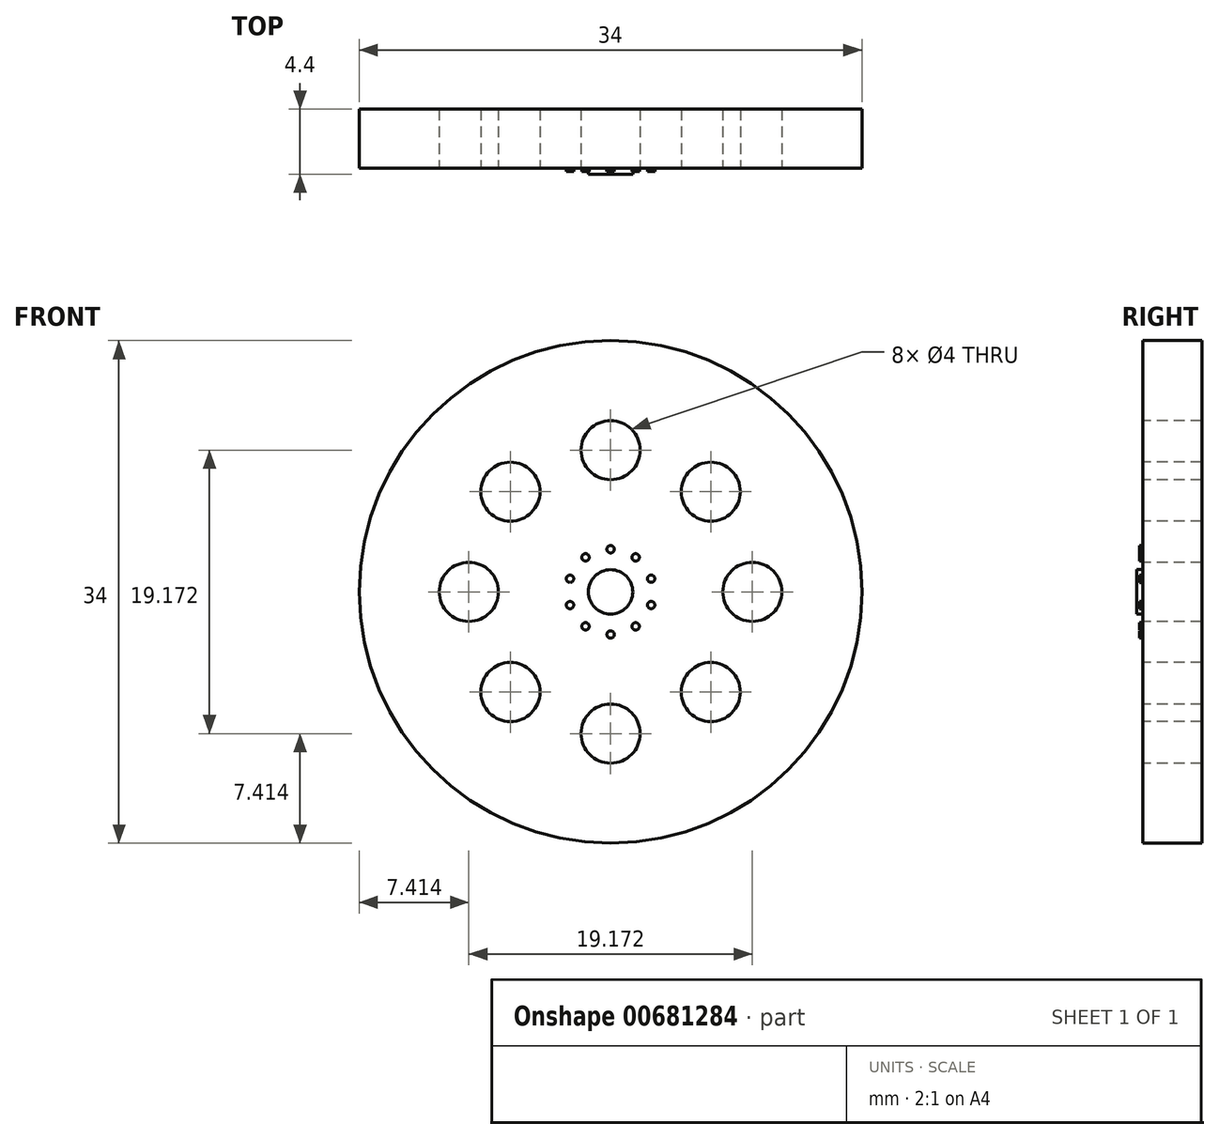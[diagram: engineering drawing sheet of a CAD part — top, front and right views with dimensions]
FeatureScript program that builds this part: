
annotation { "Feature Type Name" : "Feature", "Feature Type Description" : "" }
export const myFeature = defineFeature(function(context is Context, id is Id, definition is map)
    precondition{}
    {
        {
            var Q0;
            Q0=qCreatedBy(makeId("Front.planeOp"),FACE);
            var sketch = newSketch(context, id + "F0", { "sketchPlane" : qUnion([Q0])});
            skCircle(sketch, "E0", {"center": v(0, 0) * mm, "radius": 17 * mm});
            skSolve(sketch);
        }
        {
            var Q0;
            Q0 = qSketchRegion(id + "F0", true);
            extrude(context, id + "F1", {"entities" : qUnion([Q0]), "endBound" : BoundingType.SYMMETRIC, "depth" : 4 * mm, "offsetDistance" : 25 * mm});
        }
        {
            var Q0;
            Q0=makeQuery(id+"F1.opExtrude","CAP_FACE",FACE,{"disambiguationData":[OSD([sQuery(id+"F0.wireOp",EDGE,"E0")])],"isStart":false});
            var sketch = newSketch(context, id + "F2", { "sketchPlane" : qUnion([Q0])});
            skCircle(sketch, "E1", {"center": v(0, 9.59) * mm, "radius": 2 * mm});
            skCircle(sketch, "E2.1.0", {"center": v(-6.78, 6.78) * mm, "radius": 2 * mm});
            skCircle(sketch, "E2.2.0", {"center": v(-9.59, 0) * mm, "radius": 2 * mm});
            skCircle(sketch, "E2.3.0", {"center": v(-6.78, -6.78) * mm, "radius": 2 * mm});
            skCircle(sketch, "E2.4.0", {"center": v(0, -9.59) * mm, "radius": 2 * mm});
            skCircle(sketch, "E2.5.0", {"center": v(6.78, -6.78) * mm, "radius": 2 * mm});
            skCircle(sketch, "E2.6.0", {"center": v(9.59, 0) * mm, "radius": 2 * mm});
            skCircle(sketch, "E2.7.0", {"center": v(6.78, 6.78) * mm, "radius": 2 * mm});
            skPoint(sketch, "E2.center", {"position": v(0, 0) * mm});
            skSolve(sketch);
        }
        {
            var Q0;
            Q0=makeQuery(id+"F2.imprint","IMPRINT",FACE,{"disambiguationData":[TD([[makeQuery(id+"F2.imprint","IMPRINT",EDGE,{"derivedFrom":sQuery(id+"F2.wireOp",EDGE,"E2.1.0")}),1.0]])]});
            var Q1;
            Q1=makeQuery(id+"F2.imprint","IMPRINT",FACE,{"disambiguationData":[TD([[makeQuery(id+"F2.imprint","IMPRINT",EDGE,{"derivedFrom":sQuery(id+"F2.wireOp",EDGE,"E2.2.0")}),1.0]])]});
            var Q2;
            Q2=makeQuery(id+"F2.imprint","IMPRINT",FACE,{"disambiguationData":[TD([[makeQuery(id+"F2.imprint","IMPRINT",EDGE,{"derivedFrom":sQuery(id+"F2.wireOp",EDGE,"E2.3.0")}),1.0]])]});
            var Q3;
            Q3=makeQuery(id+"F2.imprint","IMPRINT",FACE,{"disambiguationData":[TD([[makeQuery(id+"F2.imprint","IMPRINT",EDGE,{"derivedFrom":sQuery(id+"F2.wireOp",EDGE,"E2.4.0")}),1.0]])]});
            var Q4;
            Q4=makeQuery(id+"F2.imprint","IMPRINT",FACE,{"disambiguationData":[TD([[makeQuery(id+"F2.imprint","IMPRINT",EDGE,{"derivedFrom":sQuery(id+"F2.wireOp",EDGE,"E2.5.0")}),1.0]])]});
            var Q5;
            Q5=makeQuery(id+"F2.imprint","IMPRINT",FACE,{"disambiguationData":[TD([[makeQuery(id+"F2.imprint","IMPRINT",EDGE,{"derivedFrom":sQuery(id+"F2.wireOp",EDGE,"E2.6.0")}),1.0]])]});
            var Q6;
            Q6=makeQuery(id+"F2.imprint","IMPRINT",FACE,{"disambiguationData":[TD([[makeQuery(id+"F2.imprint","IMPRINT",EDGE,{"derivedFrom":sQuery(id+"F2.wireOp",EDGE,"E2.7.0")}),1.0]])]});
            var Q7;
            Q7=makeQuery(id+"F2.imprint","IMPRINT",FACE,{"disambiguationData":[TD([[makeQuery(id+"F2.imprint","IMPRINT",EDGE,{"derivedFrom":sQuery(id+"F2.wireOp",EDGE,"E1")}),1.0]])]});
            extrude(context, id + "F3", {"entities" : qUnion([Q0, Q1, Q2, Q3, Q4, Q5, Q6, Q7]), "operationType" : NewBodyOperationType.REMOVE, "oppositeDirection" : true, "depth" : 4 * mm, "offsetDistance" : 25 * mm});
        }
        {
            var Q0;
            Q0=makeQuery(id+"F1.opExtrude","CAP_FACE",FACE,{"disambiguationData":[OSD([sQuery(id+"F0.wireOp",EDGE,"E0")])],"isStart":false});
            var sketch = newSketch(context, id + "F4", { "sketchPlane" : qUnion([Q0])});
            skCircle(sketch, "E3", {"center": v(0, 0) * mm, "radius": 1.84 * mm});
            skCircle(sketch, "E4", {"center": v(0, 2.88) * mm, "radius": 0.25 * mm});
            skCircle(sketch, "E5.1.0", {"center": v(-1.7, 2.33) * mm, "radius": 0.25 * mm});
            skCircle(sketch, "E5.2.0", {"center": v(-2.74, 0.9) * mm, "radius": 0.25 * mm});
            skCircle(sketch, "E5.3.0", {"center": v(-2.74, -0.9) * mm, "radius": 0.25 * mm});
            skCircle(sketch, "E5.4.0", {"center": v(-1.7, -2.33) * mm, "radius": 0.25 * mm});
            skCircle(sketch, "E5.5.0", {"center": v(0, -2.88) * mm, "radius": 0.25 * mm});
            skCircle(sketch, "E5.6.0", {"center": v(1.7, -2.33) * mm, "radius": 0.25 * mm});
            skCircle(sketch, "E5.7.0", {"center": v(2.74, -0.9) * mm, "radius": 0.25 * mm});
            skCircle(sketch, "E5.8.0", {"center": v(2.74, 0.9) * mm, "radius": 0.25 * mm});
            skCircle(sketch, "E5.9.0", {"center": v(1.7, 2.33) * mm, "radius": 0.25 * mm});
            skSolve(sketch);
        }
        {
            var Q0;
            Q0=makeQuery(id+"F4.imprint","IMPRINT",FACE,{"disambiguationData":[TD([[makeQuery(id+"F4.imprint","IMPRINT",EDGE,{"derivedFrom":sQuery(id+"F4.wireOp",EDGE,"E5.2.0")}),1.0]])]});
            var Q1;
            Q1=makeQuery(id+"F4.imprint","IMPRINT",FACE,{"disambiguationData":[TD([[makeQuery(id+"F4.imprint","IMPRINT",EDGE,{"derivedFrom":sQuery(id+"F4.wireOp",EDGE,"E5.3.0")}),1.0]])]});
            var Q2;
            Q2=makeQuery(id+"F4.imprint","IMPRINT",FACE,{"disambiguationData":[TD([[makeQuery(id+"F4.imprint","IMPRINT",EDGE,{"derivedFrom":sQuery(id+"F4.wireOp",EDGE,"E5.4.0")}),1.0]])]});
            var Q3;
            Q3=makeQuery(id+"F4.imprint","IMPRINT",FACE,{"disambiguationData":[TD([[makeQuery(id+"F4.imprint","IMPRINT",EDGE,{"derivedFrom":sQuery(id+"F4.wireOp",EDGE,"E5.5.0")}),1.0]])]});
            var Q4;
            Q4=makeQuery(id+"F4.imprint","IMPRINT",FACE,{"disambiguationData":[TD([[makeQuery(id+"F4.imprint","IMPRINT",EDGE,{"derivedFrom":sQuery(id+"F4.wireOp",EDGE,"E5.6.0")}),1.0]])]});
            var Q5;
            Q5=makeQuery(id+"F4.imprint","IMPRINT",FACE,{"disambiguationData":[TD([[makeQuery(id+"F4.imprint","IMPRINT",EDGE,{"derivedFrom":sQuery(id+"F4.wireOp",EDGE,"E5.7.0")}),1.0]])]});
            var Q6;
            Q6=makeQuery(id+"F4.imprint","IMPRINT",FACE,{"disambiguationData":[TD([[makeQuery(id+"F4.imprint","IMPRINT",EDGE,{"derivedFrom":sQuery(id+"F4.wireOp",EDGE,"E5.8.0")}),1.0]])]});
            var Q7;
            Q7=makeQuery(id+"F4.imprint","IMPRINT",FACE,{"disambiguationData":[TD([[makeQuery(id+"F4.imprint","IMPRINT",EDGE,{"derivedFrom":sQuery(id+"F4.wireOp",EDGE,"E5.9.0")}),1.0]])]});
            var Q8;
            Q8=makeQuery(id+"F4.imprint","IMPRINT",FACE,{"disambiguationData":[TD([[makeQuery(id+"F4.imprint","IMPRINT",EDGE,{"derivedFrom":sQuery(id+"F4.wireOp",EDGE,"E4")}),1.0]])]});
            var Q9;
            Q9=makeQuery(id+"F4.imprint","IMPRINT",FACE,{"disambiguationData":[TD([[makeQuery(id+"F4.imprint","IMPRINT",EDGE,{"derivedFrom":sQuery(id+"F4.wireOp",EDGE,"E5.1.0")}),1.0]])]});
            extrude(context, id + "F5", {"entities" : qUnion([Q0, Q1, Q2, Q3, Q4, Q5, Q6, Q7, Q8, Q9]), "operationType" : NewBodyOperationType.ADD, "depth" : .2 * mm, "offsetDistance" : 25 * mm});
        }
        {
            var Q0;
            Q0=makeQuery(id+"F1.opExtrude","CAP_FACE",FACE,{"disambiguationData":[OSD([sQuery(id+"F0.wireOp",EDGE,"E0")])],"isStart":false});
            var sketch = newSketch(context, id + "F6", { "sketchPlane" : qUnion([Q0])});
            skCircle(sketch, "E6", {"center": v(0, 0) * mm, "radius": 1.5 * mm});
            skSolve(sketch);
        }
        {
            var Q0;
            Q0=makeQuery(id+"F6.imprint","IMPRINT",FACE,{"disambiguationData":[TD([[makeQuery(id+"F6.imprint","IMPRINT",EDGE,{"derivedFrom":sQuery(id+"F6.wireOp",EDGE,"E6")}),1.0]])]});
            extrude(context, id + "F7", {"entities" : qUnion([Q0]), "operationType" : NewBodyOperationType.ADD, "depth" : .4 * mm, "offsetDistance" : 25 * mm});
        }
    });
